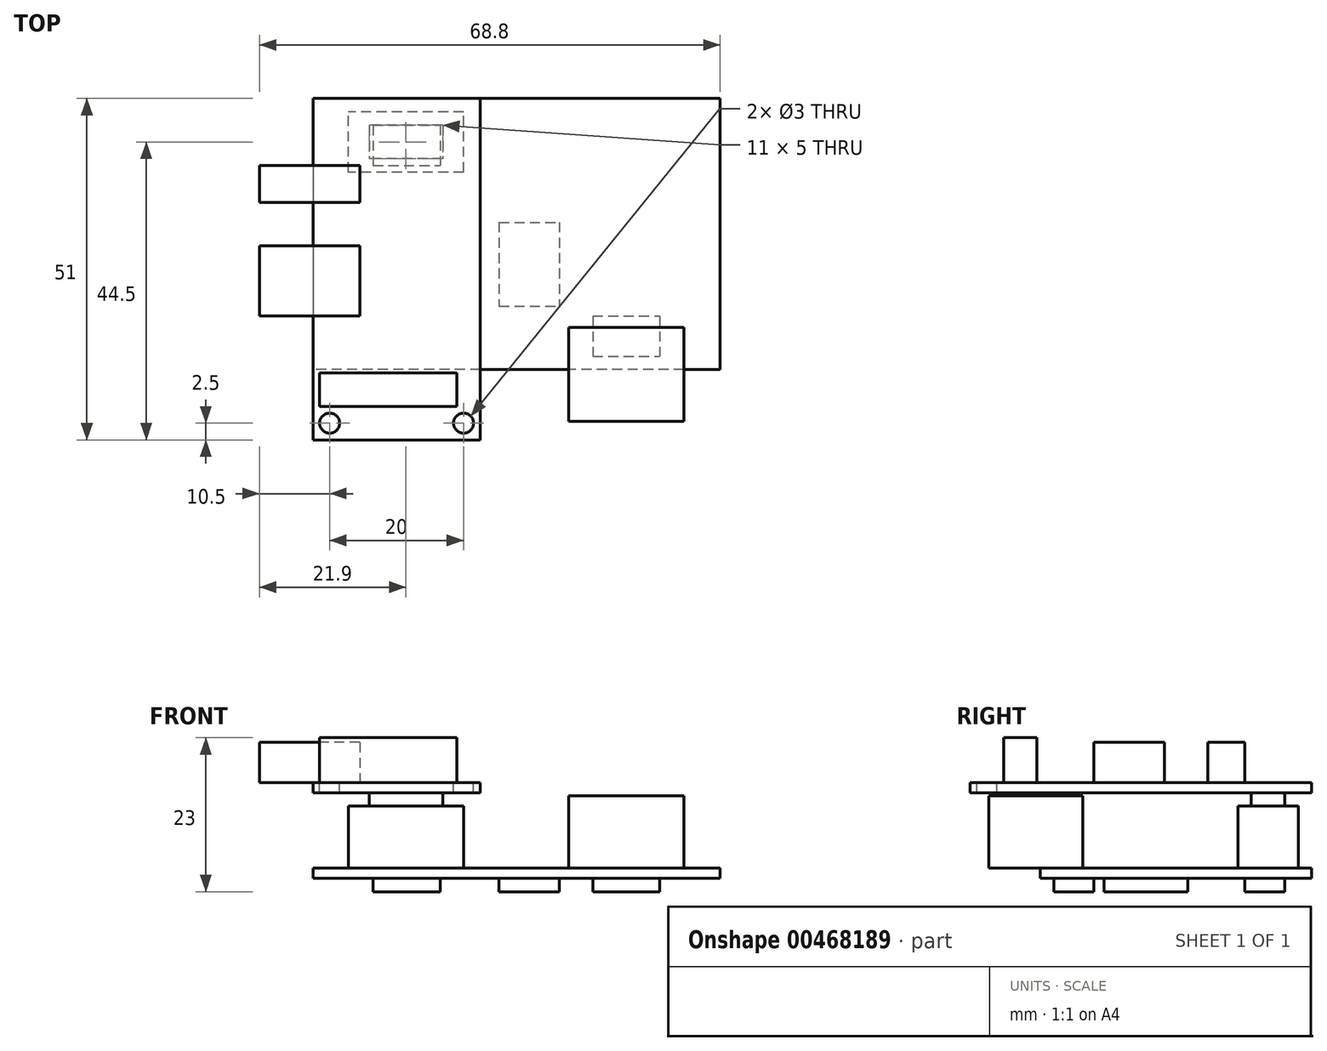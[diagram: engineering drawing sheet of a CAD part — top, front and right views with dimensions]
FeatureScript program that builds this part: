
annotation { "Feature Type Name" : "Feature", "Feature Type Description" : "" }
export const myFeature = defineFeature(function(context is Context, id is Id, definition is map)
    precondition{}
    {
        {
            var Q0;
            Q0=qCreatedBy(makeId("Top.planeOp"),FACE);
            var sketch = newSketch(context, id + "F0", { "sketchPlane" : qUnion([Q0])});
            skLineSegment(sketch, "E0.bottom", {"start": v(30.4, 20.25) * mm, "end": v(-30.4, 20.25) * mm});
            skLineSegment(sketch, "E0.top", {"start": v(30.4, -20.25) * mm, "end": v(-30.4, -20.25) * mm});
            skLineSegment(sketch, "E0.left", {"start": v(30.4, 20.25) * mm, "end": v(30.4, -20.25) * mm});
            skLineSegment(sketch, "E0.right", {"start": v(-30.4, 20.25) * mm, "end": v(-30.4, -20.25) * mm});
            skPoint(sketch, "E0.middle", {"position": v(0, 0) * mm});
            skLineSegment(sketch, "E1", {"start": v(-42.92, 0) * mm, "end": v(50.86, 0) * mm, "construction": true});
            skPoint(sketch, "E1.endSnap0", {"position": v(-30.4, 0) * mm});
            skLineSegment(sketch, "E2", {"start": v(0, 28.72) * mm, "end": v(0, -27.65) * mm, "construction": true});
            skPoint(sketch, "E2.endSnap0", {"position": v(0, -20.25) * mm});
            skSolve(sketch);
        }
        {
            var Q0;
            Q0=makeQuery(id+"F0.imprint","IMPRINT",FACE,{"disambiguationData":[TD([[makeQuery(id+"F0.imprint","IMPRINT",EDGE,{"derivedFrom":sQuery(id+"F0.wireOp",EDGE,"E0.bottom")}),1.0]])]});
            extrude(context, id + "F1", {"entities" : qUnion([Q0]), "depth" : 1.5 * mm});
        }
        {
            var Q0;
            Q0=makeQuery(id+"F1.opExtrude","CAP_FACE",FACE,{"disambiguationData":[OSD([sQuery(id+"F0.wireOp",EDGE,"E0.bottom"),sQuery(id+"F0.wireOp",EDGE,"E0.top"),sQuery(id+"F0.wireOp",EDGE,"E0.left"),sQuery(id+"F0.wireOp",EDGE,"E0.right")])],"isStart":false});
            var sketch = newSketch(context, id + "F2", { "sketchPlane" : qUnion([Q0])});
            skLineSegment(sketch, "E3.bottom", {"start": v(7.8, -13.95) * mm, "end": v(25, -13.95) * mm});
            skLineSegment(sketch, "E3.top", {"start": v(7.8, -27.95) * mm, "end": v(25, -27.95) * mm});
            skLineSegment(sketch, "E3.left", {"start": v(7.8, -13.95) * mm, "end": v(7.8, -27.95) * mm});
            skLineSegment(sketch, "E3.right", {"start": v(25, -13.95) * mm, "end": v(25, -27.95) * mm});
            skSolve(sketch);
        }
        {
            var Q0;
            {var subQ0=sQuery(id+"F2.wireOp",EDGE,"E3.top");Q0=makeQuery(id+"F2.imprint","IMPRINT",FACE,{"disambiguationData":[TD([[makeQuery(id+"F2.imprint","IMPRINT",EDGE,{"derivedFrom":subQ0}),1.0]])]});}
            var Q1;
            {var subQ0=sQuery(id+"F2.wireOp",EDGE,"E3.bottom");Q1=makeQuery(id+"F2.imprint","IMPRINT",FACE,{"disambiguationData":[TD([[makeQuery(id+"F2.imprint","IMPRINT",EDGE,{"derivedFrom":subQ0}),-1.0]])]});}
            extrude(context, id + "F3", {"entities" : qUnion([Q0, Q1]), "operationType" : NewBodyOperationType.ADD, "depth" : 10.8 * mm});
        }
        {
            var Q0;
            Q0=makeQuery(id+"F1.opExtrude","CAP_FACE",FACE,{"disambiguationData":[OSD([sQuery(id+"F0.wireOp",EDGE,"E0.bottom"),sQuery(id+"F0.wireOp",EDGE,"E0.top"),sQuery(id+"F0.wireOp",EDGE,"E0.left"),sQuery(id+"F0.wireOp",EDGE,"E0.right")])],"isStart":false});
            var sketch = newSketch(context, id + "F4", { "sketchPlane" : qUnion([Q0])});
            skLineSegment(sketch, "E4.bottom", {"start": v(-7.9, 9.25) * mm, "end": v(-25.1, 9.25) * mm});
            skLineSegment(sketch, "E4.top", {"start": v(-7.9, 18.25) * mm, "end": v(-25.1, 18.25) * mm});
            skLineSegment(sketch, "E4.left", {"start": v(-7.9, 9.25) * mm, "end": v(-7.9, 18.25) * mm});
            skLineSegment(sketch, "E4.right", {"start": v(-25.1, 9.25) * mm, "end": v(-25.1, 18.25) * mm});
            skSolve(sketch);
        }
        {
            var Q0;
            Q0=makeQuery(id+"F4.imprint","IMPRINT",FACE,{"disambiguationData":[TD([[makeQuery(id+"F4.imprint","IMPRINT",EDGE,{"derivedFrom":sQuery(id+"F4.wireOp",EDGE,"E4.bottom")}),-1.0]])]});
            extrude(context, id + "F5", {"entities" : qUnion([Q0]), "operationType" : NewBodyOperationType.ADD, "depth" : 9.3 * mm});
        }
        {
            var Q0;
            Q0=makeQuery(id+"F1.opExtrude","CAP_FACE",FACE,{"disambiguationData":[OSD([sQuery(id+"F0.wireOp",EDGE,"E0.bottom"),sQuery(id+"F0.wireOp",EDGE,"E0.top"),sQuery(id+"F0.wireOp",EDGE,"E0.left"),sQuery(id+"F0.wireOp",EDGE,"E0.right")])],"isStart":true});
            var sketch = newSketch(context, id + "F6", { "sketchPlane" : qUnion([Q0])});
            skLineSegment(sketch, "E5.bottom", {"start": v(-21.4, -16.25) * mm, "end": v(-11.4, -16.25) * mm});
            skLineSegment(sketch, "E5.top", {"start": v(-21.4, -10.25) * mm, "end": v(-11.4, -10.25) * mm});
            skLineSegment(sketch, "E5.left", {"start": v(-21.4, -16.25) * mm, "end": v(-21.4, -10.25) * mm});
            skLineSegment(sketch, "E5.right", {"start": v(-11.4, -16.25) * mm, "end": v(-11.4, -10.25) * mm});
            skLineSegment(sketch, "E6.bottom", {"start": v(-2.6, -1.75) * mm, "end": v(6.4, -1.75) * mm});
            skLineSegment(sketch, "E6.top", {"start": v(-2.6, 10.75) * mm, "end": v(6.4, 10.75) * mm});
            skLineSegment(sketch, "E6.left", {"start": v(-2.6, -1.75) * mm, "end": v(-2.6, 10.75) * mm});
            skLineSegment(sketch, "E6.right", {"start": v(6.4, -1.75) * mm, "end": v(6.4, 10.75) * mm});
            skLineSegment(sketch, "E7.bottom", {"start": v(11.4, 12.25) * mm, "end": v(21.4, 12.25) * mm});
            skLineSegment(sketch, "E7.top", {"start": v(11.4, 18.25) * mm, "end": v(21.4, 18.25) * mm});
            skLineSegment(sketch, "E7.left", {"start": v(11.4, 12.25) * mm, "end": v(11.4, 18.25) * mm});
            skLineSegment(sketch, "E7.right", {"start": v(21.4, 12.25) * mm, "end": v(21.4, 18.25) * mm});
            skSolve(sketch);
        }
        {
            var Q0;
            Q0=makeQuery(id+"F6.imprint","IMPRINT",FACE,{"disambiguationData":[TD([[makeQuery(id+"F6.imprint","IMPRINT",EDGE,{"derivedFrom":sQuery(id+"F6.wireOp",EDGE,"E5.bottom")}),1.0]])]});
            var Q1;
            Q1=makeQuery(id+"F6.imprint","IMPRINT",FACE,{"disambiguationData":[TD([[makeQuery(id+"F6.imprint","IMPRINT",EDGE,{"derivedFrom":sQuery(id+"F6.wireOp",EDGE,"E6.bottom")}),1.0]])]});
            var Q2;
            Q2=makeQuery(id+"F6.imprint","IMPRINT",FACE,{"disambiguationData":[TD([[makeQuery(id+"F6.imprint","IMPRINT",EDGE,{"derivedFrom":sQuery(id+"F6.wireOp",EDGE,"E7.bottom")}),1.0]])]});
            extrude(context, id + "F7", {"entities" : qUnion([Q0, Q1, Q2]), "operationType" : NewBodyOperationType.ADD, "depth" : 2 * mm});
        }
        {
            var Q0;
            Q0=makeQuery(id+"F5.opExtrude","CAP_FACE",FACE,{"disambiguationData":[OSD([sQuery(id+"F4.wireOp",EDGE,"E4.bottom"),sQuery(id+"F4.wireOp",EDGE,"E4.top"),sQuery(id+"F4.wireOp",EDGE,"E4.left"),sQuery(id+"F4.wireOp",EDGE,"E4.right")])],"isStart":false});
            var sketch = newSketch(context, id + "F8", { "sketchPlane" : qUnion([Q0])});
            skLineSegment(sketch, "E8", {"start": v(-27.2, 13.75) * mm, "end": v(-5.5, 13.75) * mm, "construction": true});
            skPoint(sketch, "E8.startSnap0", {"position": v(-25.1, 13.75) * mm});
            skPoint(sketch, "E8.endSnap0", {"position": v(-7.9, 13.75) * mm});
            skLineSegment(sketch, "E9", {"start": v(-16.5, 22.15) * mm, "end": v(-16.5, 6.3) * mm, "construction": true});
            skPoint(sketch, "E9.startSnap0", {"position": v(-16.5, 18.25) * mm});
            skPoint(sketch, "E9.endSnap0", {"position": v(-16.5, 9.25) * mm});
            skLineSegment(sketch, "E10.bottom", {"start": v(-11, 16.25) * mm, "end": v(-22, 16.25) * mm});
            skLineSegment(sketch, "E10.top", {"start": v(-11, 11.25) * mm, "end": v(-22, 11.25) * mm});
            skLineSegment(sketch, "E10.left", {"start": v(-11, 16.25) * mm, "end": v(-11, 11.25) * mm});
            skLineSegment(sketch, "E10.right", {"start": v(-22, 16.25) * mm, "end": v(-22, 11.25) * mm});
            skPoint(sketch, "E10.middle", {"position": v(-16.5, 13.75) * mm});
            skSolve(sketch);
        }
        {
            var Q0;
            Q0=makeQuery(id+"F8.imprint","IMPRINT",FACE,{"disambiguationData":[TD([[makeQuery(id+"F8.imprint","IMPRINT",EDGE,{"derivedFrom":sQuery(id+"F8.wireOp",EDGE,"E10.bottom")}),1.0]])]});
            extrude(context, id + "F9", {"entities" : qUnion([Q0]), "operationType" : NewBodyOperationType.ADD, "depth" : 2 * mm});
        }
        {
            var Q0;
            Q0=makeQuery(id+"F9.opExtrude","CAP_FACE",FACE,{"disambiguationData":[OSD([sQuery(id+"F8.wireOp",EDGE,"E10.bottom"),sQuery(id+"F8.wireOp",EDGE,"E10.top"),sQuery(id+"F8.wireOp",EDGE,"E10.left"),sQuery(id+"F8.wireOp",EDGE,"E10.right")])],"isStart":false});
            var sketch = newSketch(context, id + "F10", { "sketchPlane" : qUnion([Q0])});
            skLineSegment(sketch, "E11.bottom", {"start": v(-30.4, 20.25) * mm, "end": v(-5.4, 20.25) * mm});
            skLineSegment(sketch, "E11.top", {"start": v(-30.4, -30.75) * mm, "end": v(-5.4, -30.75) * mm});
            skLineSegment(sketch, "E11.left", {"start": v(-30.4, 20.25) * mm, "end": v(-30.4, -30.75) * mm});
            skLineSegment(sketch, "E11.right", {"start": v(-5.4, 20.25) * mm, "end": v(-5.4, -30.75) * mm});
            skSolve(sketch);
        }
        {
            var Q0;
            Q0=makeQuery(id+"F10.imprint","IMPRINT",FACE,{"disambiguationData":[TD([[makeQuery(id+"F10.imprint","IMPRINT",EDGE,{"derivedFrom":sQuery(id+"F10.wireOp",EDGE,"E11.bottom")}),-1.0]])]});
            var Q1;
            Q1=makeQuery(id+"F10.imprint","IMPRINT",FACE,{"disambiguationData":[TD([[makeQuery(id+"F10.imprint","IMPRINT",EDGE,{"derivedFrom":makeQuery(id+"F9.opExtrude","CAP_EDGE",EDGE,{"disambiguationData":[OSD([sQuery(id+"F8.wireOp",EDGE,"E10.bottom")])],"isStart":false})}),1.0]])]});
            extrude(context, id + "F11", {"entities" : qUnion([Q0, Q1]), "operationType" : NewBodyOperationType.ADD, "depth" : 1.5 * mm});
        }
        {
            var Q0;
            Q0=makeQuery(id+"F11.opExtrude","CAP_FACE",FACE,{"disambiguationData":[OSD([sQuery(id+"F10.wireOp",EDGE,"E11.bottom"),sQuery(id+"F10.wireOp",EDGE,"E11.top"),sQuery(id+"F10.wireOp",EDGE,"E11.left"),sQuery(id+"F10.wireOp",EDGE,"E11.right")])],"isStart":false});
            var sketch = newSketch(context, id + "F12", { "sketchPlane" : qUnion([Q0])});
            skLineSegment(sketch, "E12.bottom", {"start": v(-23.4, 10.25) * mm, "end": v(-38.4, 10.25) * mm});
            skLineSegment(sketch, "E12.top", {"start": v(-23.4, 4.75) * mm, "end": v(-38.4, 4.75) * mm});
            skLineSegment(sketch, "E12.left", {"start": v(-23.4, 10.25) * mm, "end": v(-23.4, 4.75) * mm});
            skLineSegment(sketch, "E12.right", {"start": v(-38.4, 10.25) * mm, "end": v(-38.4, 4.75) * mm});
            skLineSegment(sketch, "E13.bottom", {"start": v(-23.4, -1.75) * mm, "end": v(-38.4, -1.75) * mm});
            skLineSegment(sketch, "E13.top", {"start": v(-23.4, -12.25) * mm, "end": v(-38.4, -12.25) * mm});
            skLineSegment(sketch, "E13.left", {"start": v(-23.4, -1.75) * mm, "end": v(-23.4, -12.25) * mm});
            skLineSegment(sketch, "E13.right", {"start": v(-38.4, -1.75) * mm, "end": v(-38.4, -12.25) * mm});
            skSolve(sketch);
        }
        {
            var Q0;
            {var subQ0=sQuery(id+"F12.wireOp",EDGE,"E12.right");Q0=makeQuery(id+"F12.imprint","IMPRINT",FACE,{"disambiguationData":[TD([[makeQuery(id+"F12.imprint","IMPRINT",EDGE,{"derivedFrom":subQ0}),1.0]])]});}
            var Q1;
            {var subQ0=sQuery(id+"F12.wireOp",EDGE,"E12.left");Q1=makeQuery(id+"F12.imprint","IMPRINT",FACE,{"disambiguationData":[TD([[makeQuery(id+"F12.imprint","IMPRINT",EDGE,{"derivedFrom":subQ0}),-1.0]])]});}
            var Q2;
            {var subQ0=sQuery(id+"F12.wireOp",EDGE,"E13.left");Q2=makeQuery(id+"F12.imprint","IMPRINT",FACE,{"disambiguationData":[TD([[makeQuery(id+"F12.imprint","IMPRINT",EDGE,{"derivedFrom":subQ0}),-1.0]])]});}
            var Q3;
            {var subQ0=sQuery(id+"F12.wireOp",EDGE,"E13.right");Q3=makeQuery(id+"F12.imprint","IMPRINT",FACE,{"disambiguationData":[TD([[makeQuery(id+"F12.imprint","IMPRINT",EDGE,{"derivedFrom":subQ0}),1.0]])]});}
            extrude(context, id + "F13", {"entities" : qUnion([Q0, Q1, Q2, Q3]), "operationType" : NewBodyOperationType.ADD, "depth" : 6 * mm});
        }
        {
            var Q0;
            Q0=makeQuery(id+"F11.opExtrude","CAP_FACE",FACE,{"disambiguationData":[OSD([sQuery(id+"F10.wireOp",EDGE,"E11.bottom"),sQuery(id+"F10.wireOp",EDGE,"E11.top"),sQuery(id+"F10.wireOp",EDGE,"E11.left"),sQuery(id+"F10.wireOp",EDGE,"E11.right")])],"isStart":false});
            var sketch = newSketch(context, id + "F14", { "sketchPlane" : qUnion([Q0])});
            skLineSegment(sketch, "E14.bottom", {"start": v(-8.9, -20.75) * mm, "end": v(-29.4, -20.75) * mm});
            skLineSegment(sketch, "E14.top", {"start": v(-8.9, -25.75) * mm, "end": v(-29.4, -25.75) * mm});
            skLineSegment(sketch, "E14.left", {"start": v(-8.9, -20.75) * mm, "end": v(-8.9, -25.75) * mm});
            skLineSegment(sketch, "E14.right", {"start": v(-29.4, -20.75) * mm, "end": v(-29.4, -25.75) * mm});
            skSolve(sketch);
        }
        {
            var Q0;
            Q0=makeQuery(id+"F14.imprint","IMPRINT",FACE,{"disambiguationData":[TD([[makeQuery(id+"F14.imprint","IMPRINT",EDGE,{"derivedFrom":sQuery(id+"F14.wireOp",EDGE,"E14.bottom")}),1.0]])]});
            extrude(context, id + "F15", {"entities" : qUnion([Q0]), "operationType" : NewBodyOperationType.ADD, "depth" : 6.7 * mm});
        }
        {
            var Q0;
            Q0=makeQuery(id+"F11.opExtrude","CAP_FACE",FACE,{"disambiguationData":[OSD([sQuery(id+"F10.wireOp",EDGE,"E11.bottom"),sQuery(id+"F10.wireOp",EDGE,"E11.top"),sQuery(id+"F10.wireOp",EDGE,"E11.left"),sQuery(id+"F10.wireOp",EDGE,"E11.right")])],"isStart":false});
            var sketch = newSketch(context, id + "F16", { "sketchPlane" : qUnion([Q0])});
            skPoint(sketch, "E15", {"position": v(-27.9, -28.25) * mm});
            skPoint(sketch, "E16", {"position": v(-7.9, -28.25) * mm});
            skSolve(sketch);
        }
        {
            var Q0;
            Q0=sQuery(id+"F16.wireOp",VERTEX,"E16");
            var Q1;
            Q1=sQuery(id+"F16.wireOp",VERTEX,"E15");
            var Q2;
            Q2=makeQuery(id+"F1.opExtrude","SWEPT_BODY",BODY,{"disambiguationData":[OSD([sQuery(id+"F0.wireOp",EDGE,"E0.bottom"),sQuery(id+"F0.wireOp",EDGE,"E0.top"),sQuery(id+"F0.wireOp",EDGE,"E0.left"),sQuery(id+"F0.wireOp",EDGE,"E0.right")])]});
            hole(context, id + "F17", {"style" : HoleStyle.SIMPLE, "endStyle" : HoleEndStyle.THROUGH, "holeDiameter" : 3 * mm, "isTappedThrough" : true, "tappedDepth" : 12 * mm, "tapClearance" : 3, "locations" : qUnion([Q0, Q1]), "scope" : qUnion([Q2])});
        }
    });
